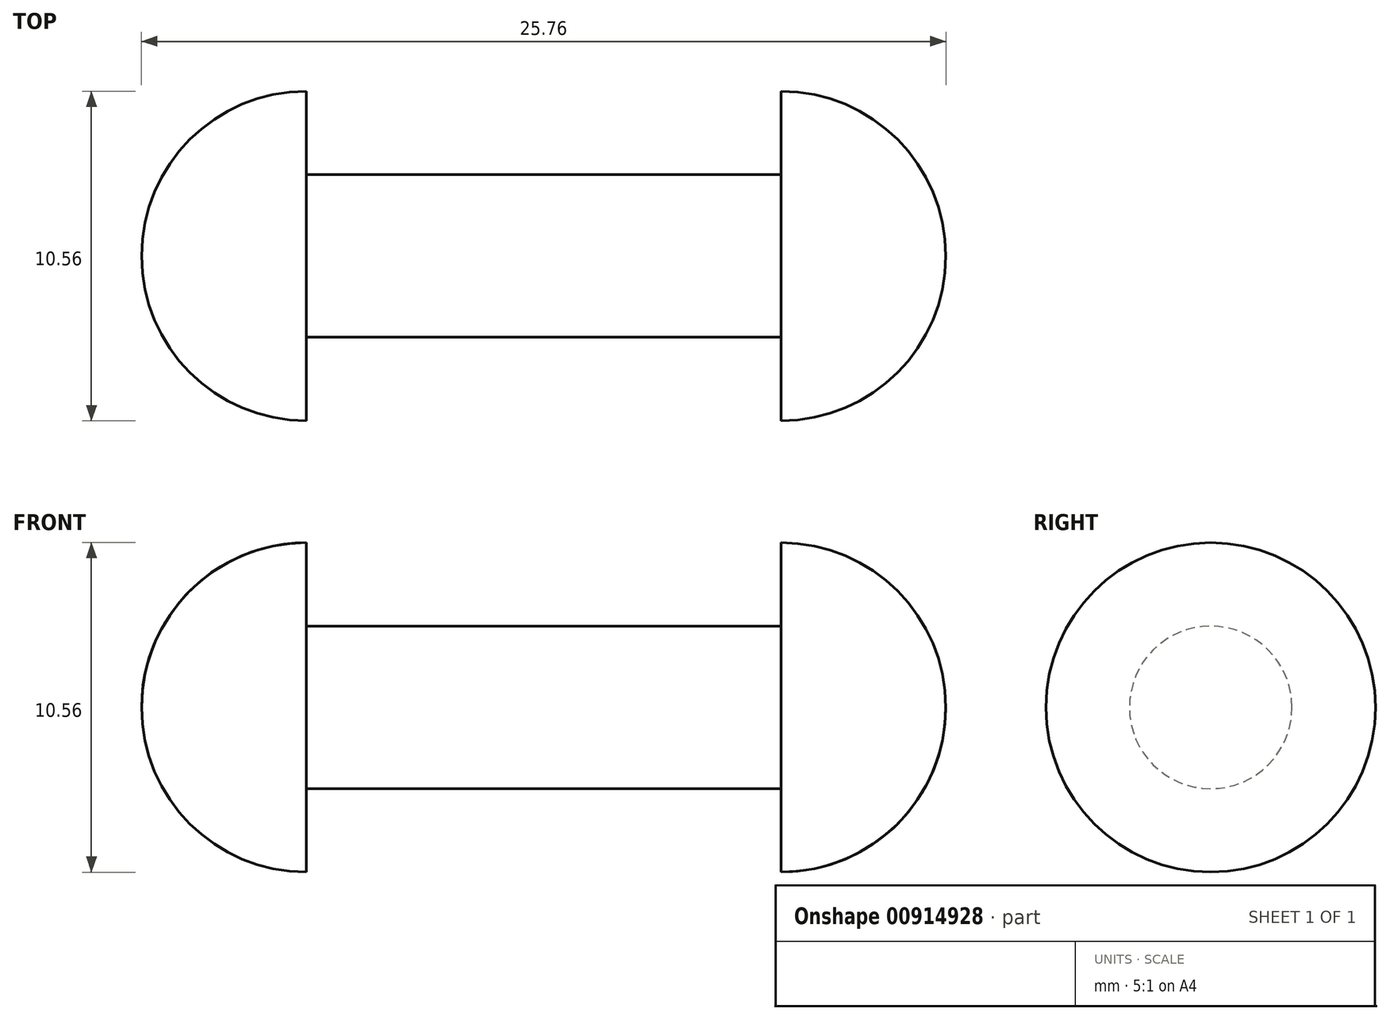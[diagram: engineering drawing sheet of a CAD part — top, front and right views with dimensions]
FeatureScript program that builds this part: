
annotation { "Feature Type Name" : "Feature", "Feature Type Description" : "" }
export const myFeature = defineFeature(function(context is Context, id is Id, definition is map)
    precondition{}
    {
        {
            var Q0;
            Q0=qCreatedBy(makeId("Front.planeOp"),FACE);
            var sketch = newSketch(context, id + "F0", { "sketchPlane" : qUnion([Q0])});
            skLineSegment(sketch, "E0.bottom", {"start": v(-7.6, 2.6) * mm, "end": v(7.6, 2.6) * mm});
            skLineSegment(sketch, "E0.top", {"start": v(-7.6, -2.6) * mm, "end": v(7.6, -2.6) * mm});
            skLineSegment(sketch, "E0.left", {"start": v(-7.6, 2.6) * mm, "end": v(-7.6, -2.6) * mm});
            skLineSegment(sketch, "E0.right", {"start": v(7.6, 2.6) * mm, "end": v(7.6, -2.6) * mm});
            skPoint(sketch, "E0.middle", {"position": v(0, 0) * mm});
            skArc(sketch, "E1", {"start": v(7.6, -5.28) * mm, "mid": v(12.88, 0) * mm, "end": v(7.6, 5.28) * mm});
            skLineSegment(sketch, "E2", {"start": v(7.6, 2.6) * mm, "end": v(7.6, 5.28) * mm});
            skLineSegment(sketch, "E3", {"start": v(7.6, -2.6) * mm, "end": v(7.6, -5.28) * mm});
            skLineSegment(sketch, "E4", {"start": v(-7.6, 2.6) * mm, "end": v(-7.6, 5.28) * mm});
            skLineSegment(sketch, "E5", {"start": v(-7.6, 5.28) * mm, "end": v(-7.6, -5.28) * mm});
            skArc(sketch, "E6", {"start": v(-7.6, 5.28) * mm, "mid": v(-12.88, 0) * mm, "end": v(-7.6, -5.28) * mm});
            skLineSegment(sketch, "E7", {"start": v(-12.88, 0) * mm, "end": v(12.88, 0) * mm});
            skSolve(sketch);
        }
        {
            var Q0;
            {var subQ0=sQuery(id+"F0.wireOp",EDGE,"E4");Q0=makeQuery(id+"F0.imprint","IMPRINT",FACE,{"disambiguationData":[TD([[makeQuery(id+"F0.imprint","IMPRINT",EDGE,{"derivedFrom":subQ0}),1.0]])]});}
            var Q1;
            {var subQ0=sQuery(id+"F0.wireOp",EDGE,"E0.bottom");Q1=makeQuery(id+"F0.imprint","IMPRINT",FACE,{"disambiguationData":[TD([[makeQuery(id+"F0.imprint","IMPRINT",EDGE,{"derivedFrom":subQ0}),-1.0]])]});}
            var Q2;
            {var subQ0=sQuery(id+"F0.wireOp",EDGE,"E2");Q2=makeQuery(id+"F0.imprint","IMPRINT",FACE,{"disambiguationData":[TD([[makeQuery(id+"F0.imprint","IMPRINT",EDGE,{"derivedFrom":subQ0}),-1.0]])]});}
            var Q3;
            Q3=sQuery(id+"F0.wireOp",EDGE,"E7");
            revolve(context, id + "F1", {"surfaceOperationType" : NewSurfaceOperationType.NEW, "entities" : qUnion([Q0, Q1, Q2]), "axis" : qUnion([Q3]), "revolveType" : RevolveType.FULL});
        }
    });
